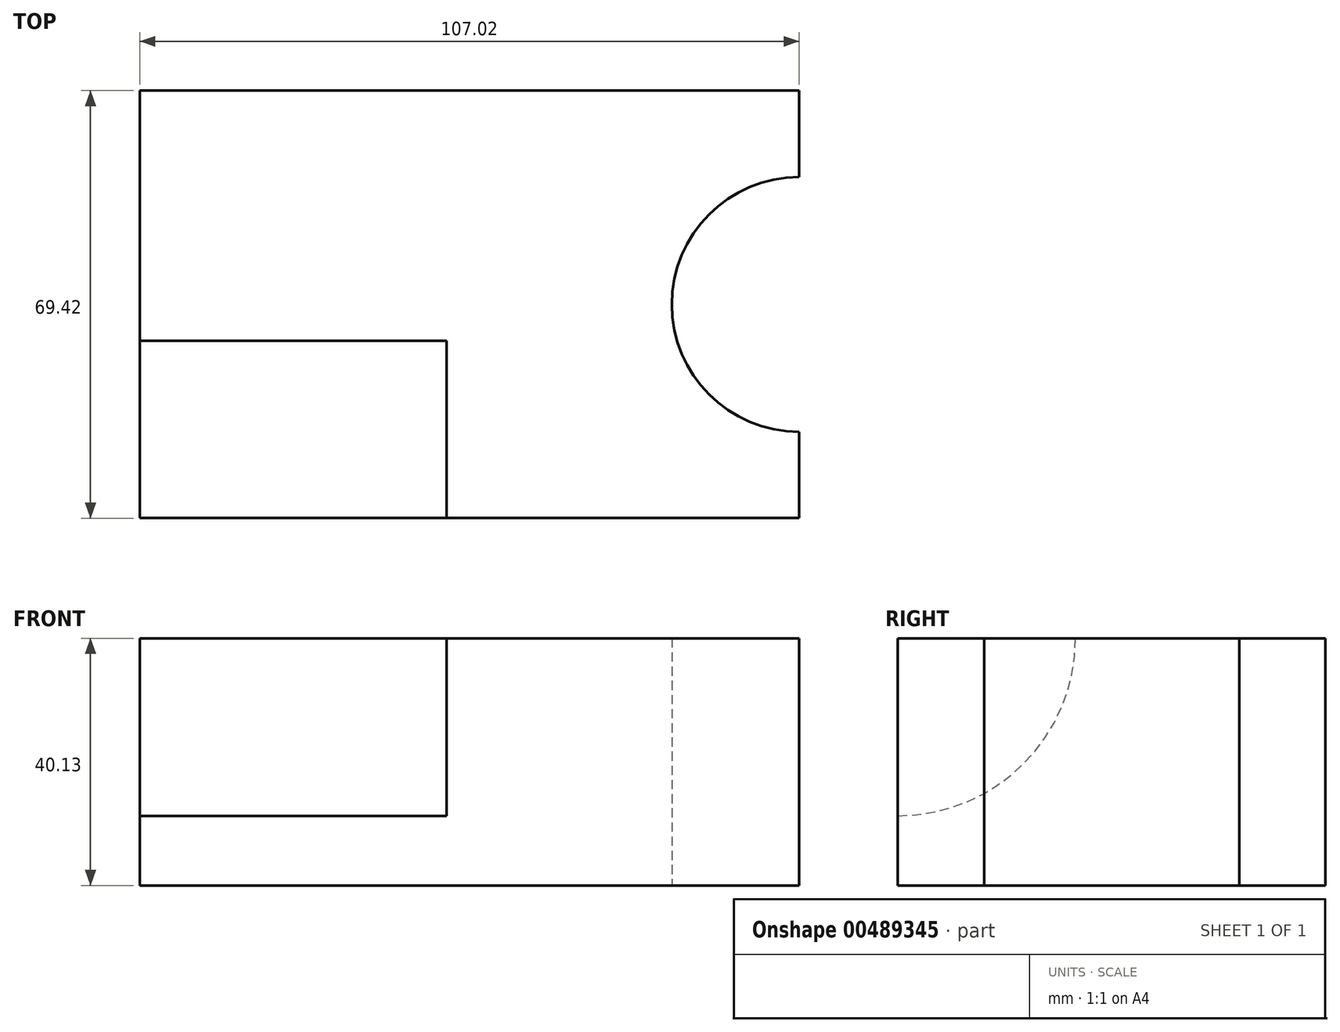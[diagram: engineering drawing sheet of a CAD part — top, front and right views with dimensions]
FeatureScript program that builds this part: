
annotation { "Feature Type Name" : "Feature", "Feature Type Description" : "" }
export const myFeature = defineFeature(function(context is Context, id is Id, definition is map)
    precondition{}
    {
        {
            var Q0;
            Q0=qCreatedBy(makeId("Top.planeOp"),FACE);
            var sketch = newSketch(context, id + "F0", { "sketchPlane" : qUnion([Q0])});
            skLineSegment(sketch, "E0.bottom", {"start": v(53.5, -34.7) * mm, "end": v(-53.5, -34.7) * mm});
            skLineSegment(sketch, "E0.top", {"start": v(53.5, 34.7) * mm, "end": v(-53.5, 34.7) * mm});
            skLineSegment(sketch, "E0.left", {"start": v(53.5, -34.7) * mm, "end": v(53.5, 34.7) * mm});
            skLineSegment(sketch, "E0.right", {"start": v(-53.5, -34.7) * mm, "end": v(-53.5, 34.7) * mm});
            skPoint(sketch, "E0.middle", {"position": v(0, 0) * mm});
            skCircle(sketch, "E1", {"center": v(53.5, 0) * mm, "radius": 20.68 * mm});
            skSolve(sketch);
        }
        {
            var Q0;
            {var subQ4=sQuery(id+"F0.wireOp",EDGE,"E0.bottom");Q0=makeQuery(id+"F0.imprint","IMPRINT",FACE,{"disambiguationData":[TD([[makeQuery(id+"F0.imprint","IMPRINT",EDGE,{"derivedFrom":subQ4}),-1.0]])]});}
            var Q1;
            {var subQ4=sQuery(id+"F0.wireOp",EDGE,"E0.bottom");Q1=makeQuery(id+"F0.imprint","IMPRINT",FACE,{"disambiguationData":[TD([[makeQuery(id+"F0.imprint","IMPRINT",EDGE,{"derivedFrom":subQ4}),-1.0]])]});}
            extrude(context, id + "F1", {"entities" : qUnion([Q0, Q1]), "depth" : 40.13 * mm});
        }
        {
            var Q0;
            Q0=makeQuery(id+"F1.opExtrude","SWEPT_FACE",FACE,{"disambiguationData":[OSD([sQuery(id+"F0.wireOp",EDGE,"E0.right")])]});
            var sketch = newSketch(context, id + "F2", { "sketchPlane" : qUnion([Q0])});
            skCircle(sketch, "E2", {"center": v(34.7, 40.13) * mm, "radius": 28.83 * mm});
            skSolve(sketch);
        }
        {
            var Q0;
            {var subQ0=sQuery(id+"F2.wireOp",EDGE,"E2");var subQ1=sQuery(id+"F0.wireOp",EDGE,"E0.right");var subQ4=makeQuery(id+"F1.opExtrude","CAP_EDGE",EDGE,{"disambiguationData":[OSD([subQ1])],"isStart":false});var subQ5=makeQuery(id+"F2.imprint","INTERSECT",VERTEX,{"derivedFrom":[subQ4,subQ0]});Q0=makeQuery(id+"F2.imprint","IMPRINT",FACE,{"disambiguationData":[TD([[makeQuery(id+"F2.imprint","IMPRINT",EDGE,{"disambiguationData":[TD([[subQ5,1.0]])],"derivedFrom":subQ0}),1.0]])]});}
            var Q1;
            {var subQ0=sQuery(id+"F2.wireOp",EDGE,"E2");var subQ1=sQuery(id+"F0.wireOp",EDGE,"E0.right");var subQ4=makeQuery(id+"F1.opExtrude","CAP_EDGE",EDGE,{"disambiguationData":[OSD([subQ1])],"isStart":false});var subQ5=makeQuery(id+"F2.imprint","INTERSECT",VERTEX,{"derivedFrom":[subQ4,subQ0]});Q1=makeQuery(id+"F2.imprint","IMPRINT",FACE,{"disambiguationData":[TD([[makeQuery(id+"F2.imprint","IMPRINT",EDGE,{"disambiguationData":[TD([[subQ5,-1.0]])],"derivedFrom":subQ0}),1.0]])]});}
            extrude(context, id + "F3", {"entities" : qUnion([Q0, Q1]), "operationType" : NewBodyOperationType.REMOVE, "oppositeDirection" : true, "depth" : 49.78 * mm});
        }
    });
